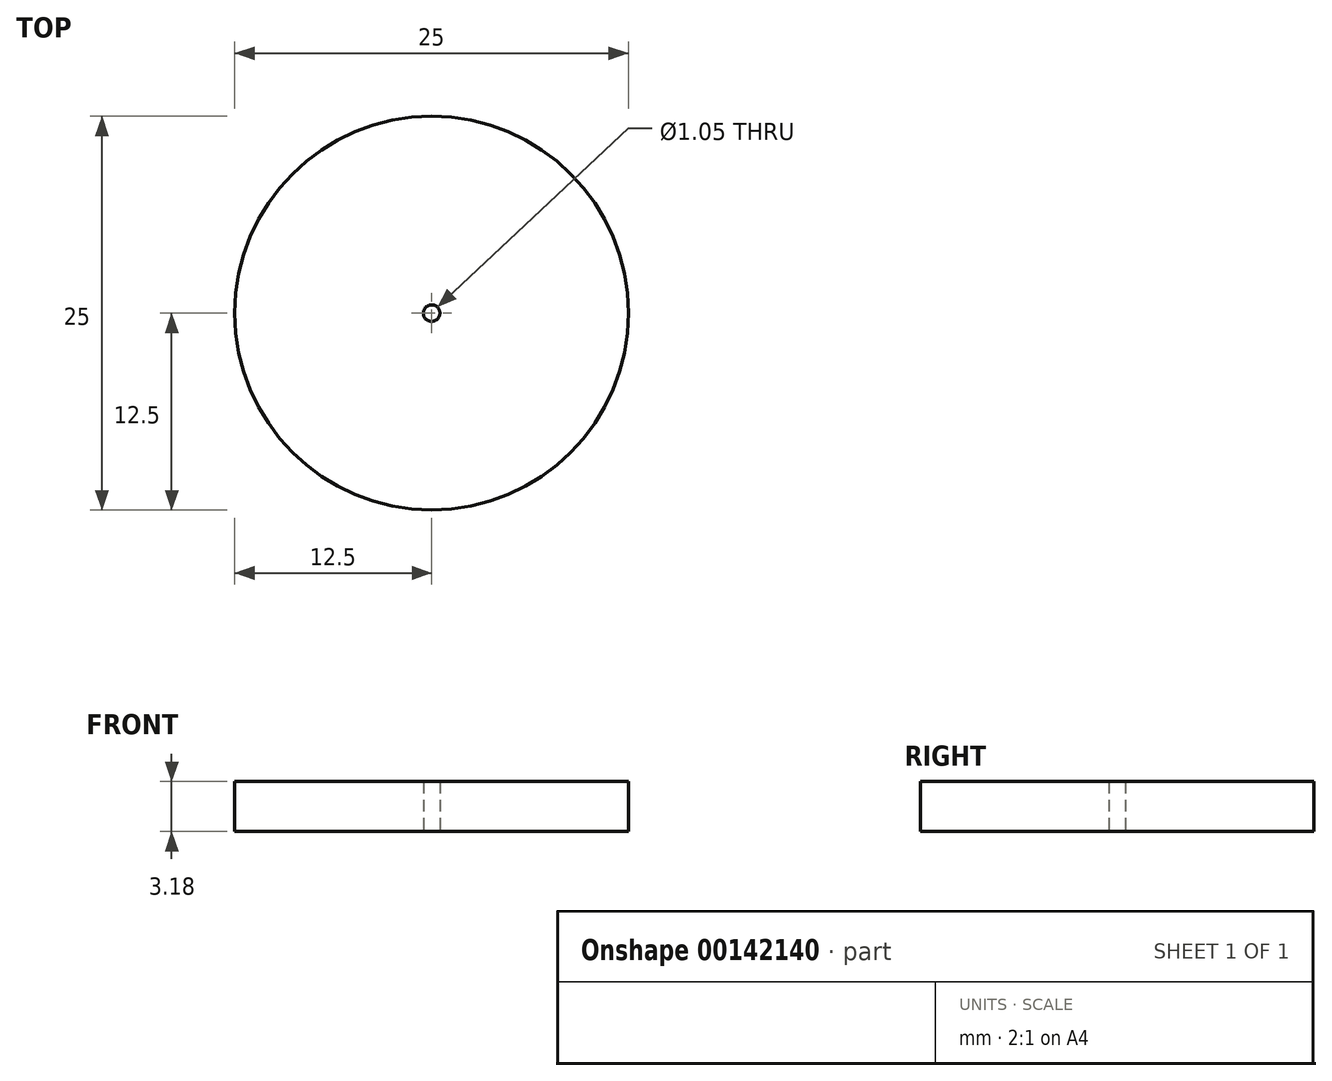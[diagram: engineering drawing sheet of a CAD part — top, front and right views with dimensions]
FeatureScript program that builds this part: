
annotation { "Feature Type Name" : "Feature", "Feature Type Description" : "" }
export const myFeature = defineFeature(function(context is Context, id is Id, definition is map)
    precondition{}
    {
        {
            var Q0;
            Q0=qCreatedBy(makeId("Top.planeOp"),FACE);
            var sketch = newSketch(context, id + "F0", { "sketchPlane" : qUnion([Q0])});
            skCircle(sketch, "E0", {"center": v(0, 0) * mm, "radius": 12.5 * mm});
            skCircle(sketch, "E1", {"center": v(0, 0) * mm, "radius": 0.53 * mm});
            skSolve(sketch);
        }
        {
            var Q0;
            Q0=makeQuery(id+"F0.imprint","IMPRINT",FACE,{"disambiguationData":[TD([[makeQuery(id+"F0.imprint","IMPRINT",EDGE,{"derivedFrom":sQuery(id+"F0.wireOp",EDGE,"E0")}),1.0]])]});
            extrude(context, id + "F1", {"entities" : qUnion([Q0]), "depth" : 3.17 * mm});
        }
    });
